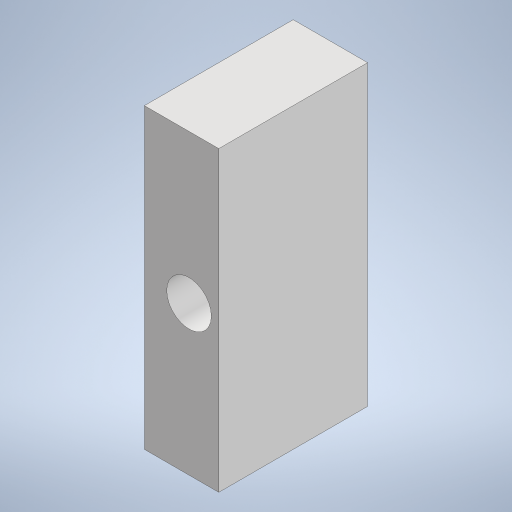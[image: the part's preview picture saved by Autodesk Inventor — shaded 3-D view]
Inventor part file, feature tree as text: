
AUTODESK INVENTOR PART (.ipt)
format: ipt  version: 2024.1 (Build 281209000, 209)  size: 206,848 bytes
history: native  units: in
note: dims shown in document units (in); Inventor stores cm internally (conversion verified against a paired STEP export)
features: extrude x2, sketch x2
ambient origin geometry x8: Origin, YZ Plane, XZ Plane, XY Plane, X Axis, Y Axis, Z Axis, Center Point
bodies: Solid1 (feature_tree)
feature tree (4):
  extrude  "Extrusion1"  Depth=0.3937in
  extrude  "Extrusion2"  Depth=0.3937in
  sketch  "Sketch1"  dims[d0=0.7874in d1=0.3937in]
  sketch  "Sketch2"  dims[d2=0.1969in d3=0.0in d4=0.1181in d5=0.0787in d6=0.3937in d7=0.0in d8=0.0in]
